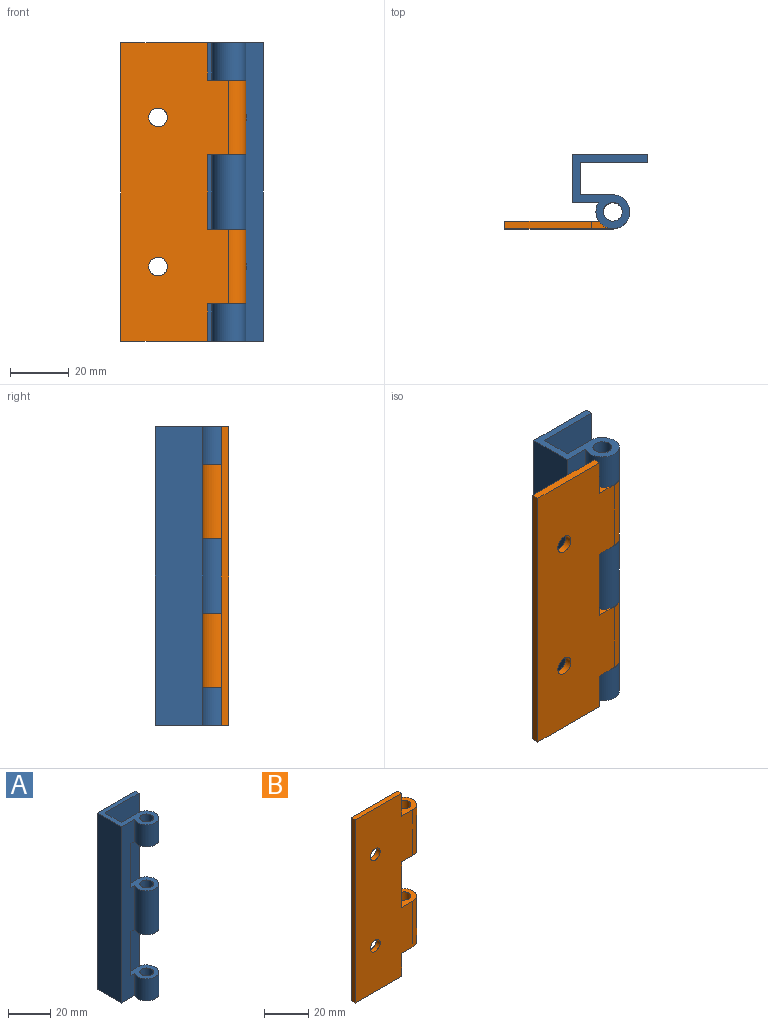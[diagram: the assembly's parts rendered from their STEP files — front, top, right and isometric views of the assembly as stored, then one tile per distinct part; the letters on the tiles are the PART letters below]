
ASSEMBLY  parts=2 mates=1
PART A: 23 faces, bbox 25.4x25.1x101.6 mm
  f0: plane 101.6x8.91mm, normal (0,-1,0), area 775mm2, adj f1,f2,f3,f9,f10,f11,f12,f13
  f1: cylinder r=5.75mm len=25.4mm, axis (0,0,-1), area 775.2mm2, adj f0,f4,f13,f15
  f2: cylinder r=5.75mm len=12.7mm, axis (0,0,-1), area 387.6mm2, adj f0,f4,f11,f12
  f3: cylinder r=5.75mm len=12.7mm, axis (0,0,-1), area 387.6mm2, adj f0,f4,f10,f16
  f4: plane 101.6x11.14mm, normal (0,1,0), area 759.4mm2, adj f1,f2,f3,f5,f10,f11,f12,f13
  f5: plane 101.6x11.05mm, normal (1,0,0), area 1122.6mm2, adj f4,f6,f10,f11
  f6: plane 101.6x22.86mm, normal (0,-1,0), area 2259.2mm2, adj f5,f7,f10,f11,f21,f22
  f7: plane 101.6x2.54mm, normal (1,0,0), area 258.1mm2, adj f6,f8,f10,f11
  f8: plane 101.6x25.4mm, normal (0,1,0), area 2517.3mm2, adj f7,f9,f10,f11,f21,f22
  f9: plane 101.6x16.13mm, normal (-1,0,0), area 1638.7mm2, adj f0,f8,f10,f11
  f10: plane 25.4x25.1mm, normal (0,0,1), area 190.3mm2, adj f0,f3,f4,f5,f6,f7,f8,f9
  f11: plane 25.4x25.1mm, normal (0,0,-1), area 190.3mm2, adj f0,f2,f4,f5,f6,f7,f8,f9
  f12: plane 13.08x11.51mm, normal (0,0,1), area 81.6mm2, adj f0,f2,f4,f14,f20
  f13: plane 13.08x11.51mm, normal (0,0,-1), area 81.6mm2, adj f0,f1,f4,f14,f19
  f14: plane 25.4x2.54mm, normal (1,0,0), area 64.5mm2, adj f0,f4,f12,f13
  f15: plane 13.08x11.51mm, normal (0,0,1), area 81.6mm2, adj f0,f1,f4,f17,f19
  f16: plane 13.08x11.51mm, normal (0,0,-1), area 81.6mm2, adj f0,f3,f4,f17,f18
  f17: plane 25.4x2.54mm, normal (1,0,0), area 64.5mm2, adj f0,f4,f15,f16
  f18: cylinder r=3.21mm len=12.7mm, axis (0,0,1), area 256.4mm2, adj f10,f16
  f19: cylinder r=3.21mm len=25.4mm, axis (0,0,1), area 512.8mm2, adj f13,f15
  f20: cylinder r=3.21mm len=12.7mm, axis (0,0,1), area 256.4mm2, adj f11,f12
  f21: cylinder r=3.17mm len=6.35mm, axis (0,1,0), area 50.7mm2, adj f6,f8
  f22: cylinder r=3.17mm len=6.35mm, axis (0,1,0), area 50.7mm2, adj f6,f8
PART B: 18 faces, bbox 42.5x11.5x101.6 mm
  f0: plane 101.6x36.79mm, normal (0,-1,0), area 3308.9mm2, adj f1,f2,f4,f5,f6,f7,f8,f9
  f1: cylinder r=5.75mm len=25.4mm, axis (0,0,-1), area 775.2mm2, adj f0,f3,f8,f12
  f2: cylinder r=5.75mm len=25.4mm, axis (0,0,-1), area 775.2mm2, adj f0,f3,f10,f13
  f3: plane 101.6x32.02mm, normal (0,1,0), area 3066.5mm2, adj f1,f2,f4,f5,f6,f7,f8,f9
  f4: plane 101.6x2.54mm, normal (-1,0,0), area 258.1mm2, adj f0,f3,f5,f6
  f5: plane 29.59x2.54mm, normal (0,0,1), area 75.2mm2, adj f0,f3,f4,f11
  f6: plane 29.59x2.54mm, normal (0,0,-1), area 75.2mm2, adj f0,f3,f4,f9
  f7: cylinder r=3.17mm len=6.35mm, axis (0,-1,0), area 50.7mm2, adj f0,f3
  f8: plane 12.95x11.51mm, normal (0,0,-1), area 81.3mm2, adj f0,f1,f3,f9,f17
  f9: plane 12.7x2.54mm, normal (1,0,0), area 32.3mm2, adj f0,f3,f6,f8
  f10: plane 12.95x11.51mm, normal (0,0,1), area 81.3mm2, adj f0,f2,f3,f11,f16
  f11: plane 12.7x2.54mm, normal (1,0,0), area 32.3mm2, adj f0,f3,f5,f10
  f12: plane 12.95x11.51mm, normal (0,0,1), area 81.3mm2, adj f0,f1,f3,f14,f17
  f13: plane 12.95x11.51mm, normal (0,0,-1), area 81.3mm2, adj f0,f2,f3,f14,f16
  f14: plane 25.4x2.54mm, normal (1,0,0), area 64.5mm2, adj f0,f3,f12,f13
  f15: cylinder r=3.17mm len=6.35mm, axis (0,-1,0), area 50.7mm2, adj f0,f3
  f16: cylinder r=3.21mm len=25.4mm, axis (0,0,1), area 512.8mm2, adj f10,f13
  f17: cylinder r=3.21mm len=25.4mm, axis (0,0,1), area 512.8mm2, adj f8,f12
PLACE A t=(0,0,50.8)mm
PLACE B rot(axis=(0,0,1),0deg) t=(0,0,50.8)mm
MATE revolute B.f1 <-> A.f1  axis (0,0,1) through (0,0,88.9)mm
